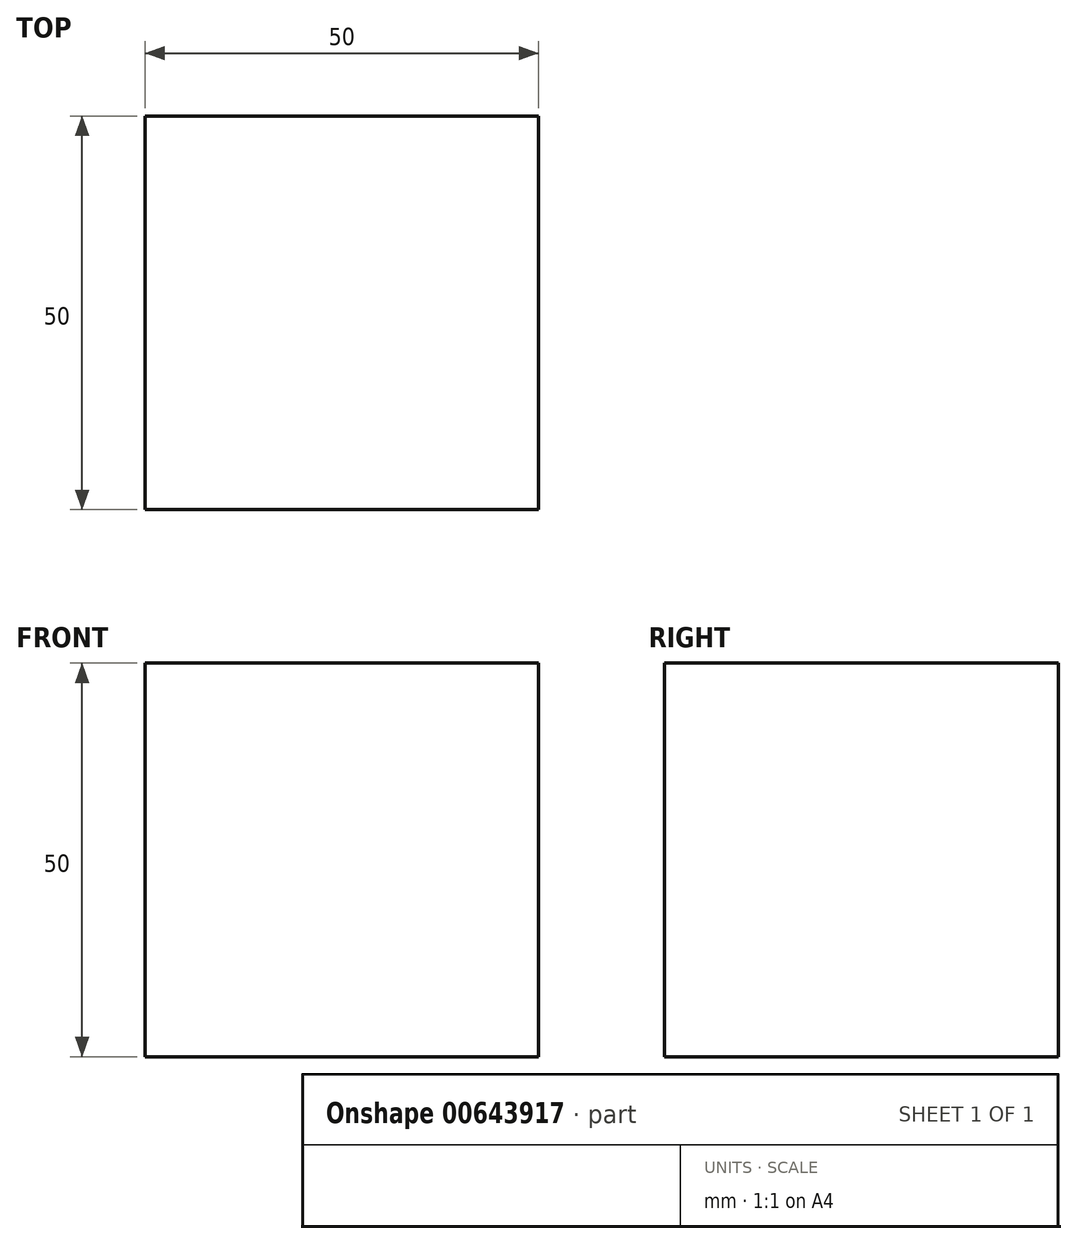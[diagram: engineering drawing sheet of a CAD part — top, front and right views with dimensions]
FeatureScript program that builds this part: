
annotation { "Feature Type Name" : "Feature", "Feature Type Description" : "" }
export const myFeature = defineFeature(function(context is Context, id is Id, definition is map)
    precondition{}
    {
        {
            var Q0;
            Q0=qCreatedBy(makeId("Top.planeOp"),FACE);
            var sketch = newSketch(context, id + "F0", { "sketchPlane" : qUnion([Q0])});
            skLineSegment(sketch, "E0.bottom", {"start": v(20.75, 23.6) * mm, "end": v(-29.25, 23.6) * mm});
            skLineSegment(sketch, "E0.top", {"start": v(20.75, -26.4) * mm, "end": v(-29.25, -26.4) * mm});
            skLineSegment(sketch, "E0.left", {"start": v(20.75, 23.6) * mm, "end": v(20.75, -26.4) * mm});
            skLineSegment(sketch, "E0.right", {"start": v(-29.25, 23.6) * mm, "end": v(-29.25, -26.4) * mm});
            skSolve(sketch);
        }
        {
            var Q0;
            Q0 = qSketchRegion(id + "F0", true);
            extrude(context, id + "F1", {"entities" : qUnion([Q0]), "depth" : 50 * mm, "offsetDistance" : 25 * mm});
        }
        {
            var Q0;
            Q0=makeQuery(id+"F1.opExtrude","CAP_FACE",FACE,{"disambiguationData":[OSD([sQuery(id+"F0.wireOp",EDGE,"E0.bottom"),sQuery(id+"F0.wireOp",EDGE,"E0.top"),sQuery(id+"F0.wireOp",EDGE,"E0.left"),sQuery(id+"F0.wireOp",EDGE,"E0.right")])],"isStart":false});
            var sketch = newSketch(context, id + "F2", { "sketchPlane" : qUnion([Q0])});
            skCircle(sketch, "E1", {"center": v(0, 0) * mm, "radius": 12.63 * mm});
            skSolve(sketch);
        }
        {
            var Q0;
            Q0 = qSketchRegion(id + "F2", true);
            extrude(context, id + "F3", {"entities" : qUnion([Q0]), "operationType" : NewBodyOperationType.ADD, "depth" : 50 * mm, "offsetDistance" : 25 * mm});
        }
        {
            var Q0;
            Q0=makeQuery(id+"F3.opExtrude","CAP_FACE",FACE,{"disambiguationData":[OSD([sQuery(id+"F2.wireOp",EDGE,"E1")])],"isStart":false});
            extrude(context, id + "F4", {"entities" : qUnion([Q0]), "operationType" : NewBodyOperationType.REMOVE, "oppositeDirection" : true, "depth" : 50 * mm, "offsetDistance" : 25 * mm});
        }
    });
